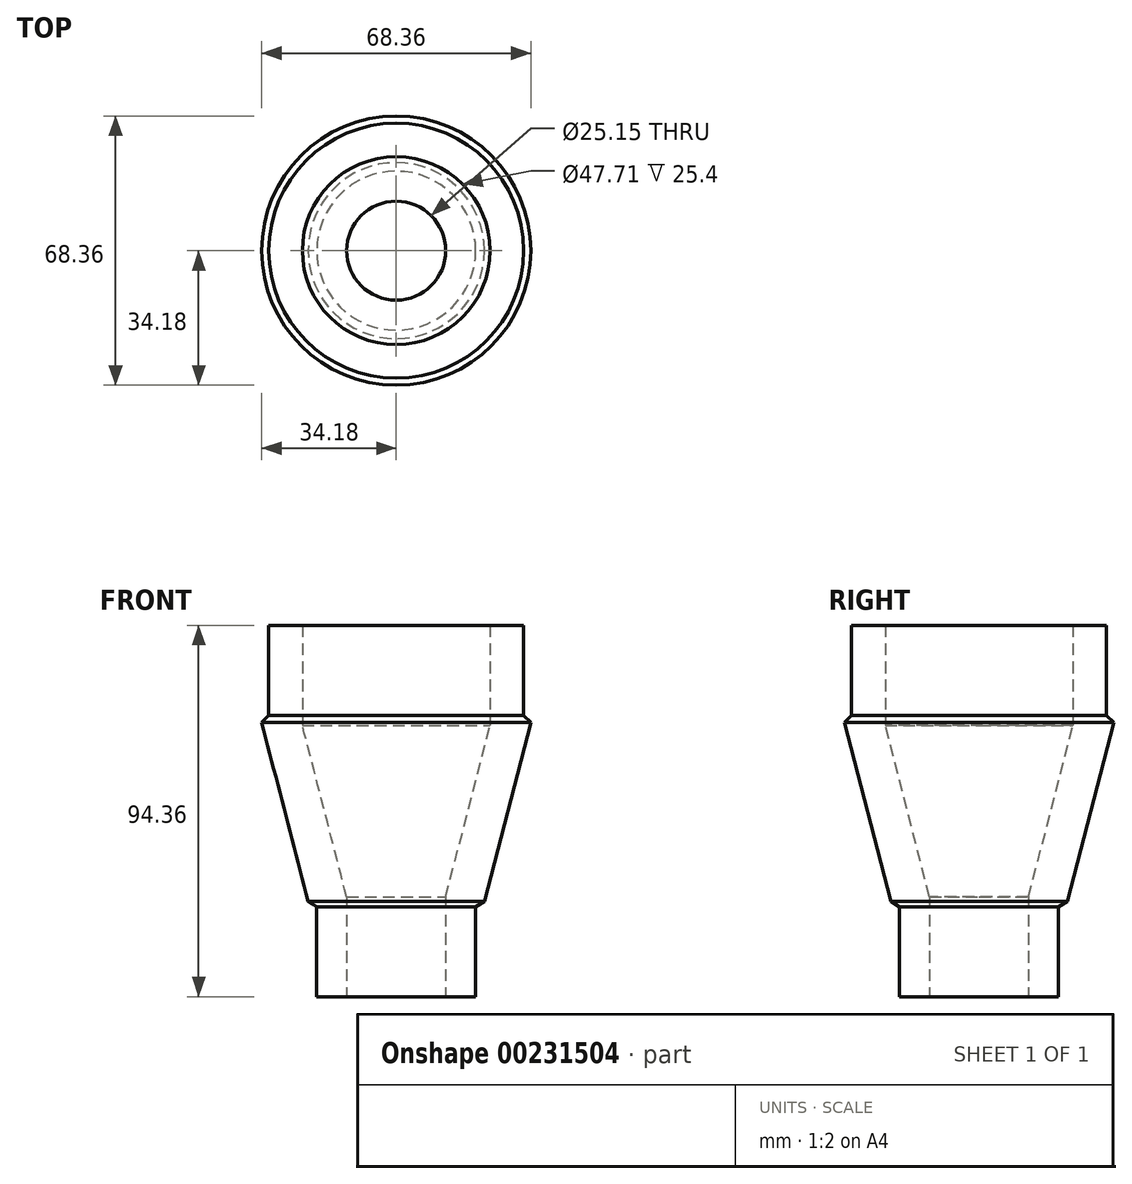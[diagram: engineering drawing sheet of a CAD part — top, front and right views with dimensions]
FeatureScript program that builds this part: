
annotation { "Feature Type Name" : "Feature", "Feature Type Description" : "" }
export const myFeature = defineFeature(function(context is Context, id is Id, definition is map)
    precondition{}
    {
        {
            var Q0;
            Q0=qCreatedBy(makeId("Front.planeOp"),FACE);
            var sketch = newSketch(context, id + "F0", { "sketchPlane" : qUnion([Q0])});
            skLineSegment(sketch, "E0", {"start": v(0, 0) * mm, "end": v(0, 50.43) * mm, "construction": true});
            skLineSegment(sketch, "E1", {"start": v(20.2, 0) * mm, "end": v(12.57, 0) * mm});
            skLineSegment(sketch, "E2", {"start": v(12.57, 0) * mm, "end": v(12.57, 25.4) * mm});
            skLineSegment(sketch, "E3", {"start": v(31.48, 94.36) * mm, "end": v(32.38, 94.36) * mm});
            skLineSegment(sketch, "E4", {"start": v(32.38, 94.36) * mm, "end": v(32.38, 71.5) * mm});
            skLineSegment(sketch, "E5", {"start": v(32.38, 71.5) * mm, "end": v(34.18, 69.7) * mm});
            skLineSegment(sketch, "E6", {"start": v(20.2, 22.86) * mm, "end": v(22.38, 24.15) * mm});
            skLineSegment(sketch, "E7", {"start": v(22.38, 24.15) * mm, "end": v(34.18, 69.7) * mm});
            skLineSegment(sketch, "E8", {"start": v(12.57, 25.4) * mm, "end": v(23.86, 68.96) * mm});
            skLineSegment(sketch, "E9", {"start": v(23.86, 68.96) * mm, "end": v(23.86, 94.36) * mm});
            skLineSegment(sketch, "E10", {"start": v(23.86, 94.36) * mm, "end": v(31.48, 94.36) * mm});
            skLineSegment(sketch, "E11", {"start": v(20.2, 22.86) * mm, "end": v(20.2, 0) * mm});
            skSolve(sketch);
        }
        {
            var Q0;
            Q0 = qSketchRegion(id + "F0", true);
            var Q1;
            Q1=sQuery(id+"F0.wireOp",EDGE,"E0");
            revolve(context, id + "F1", {"entities" : qUnion([Q0]), "axis" : qUnion([Q1]), "revolveType" : RevolveType.FULL});
        }
    });
